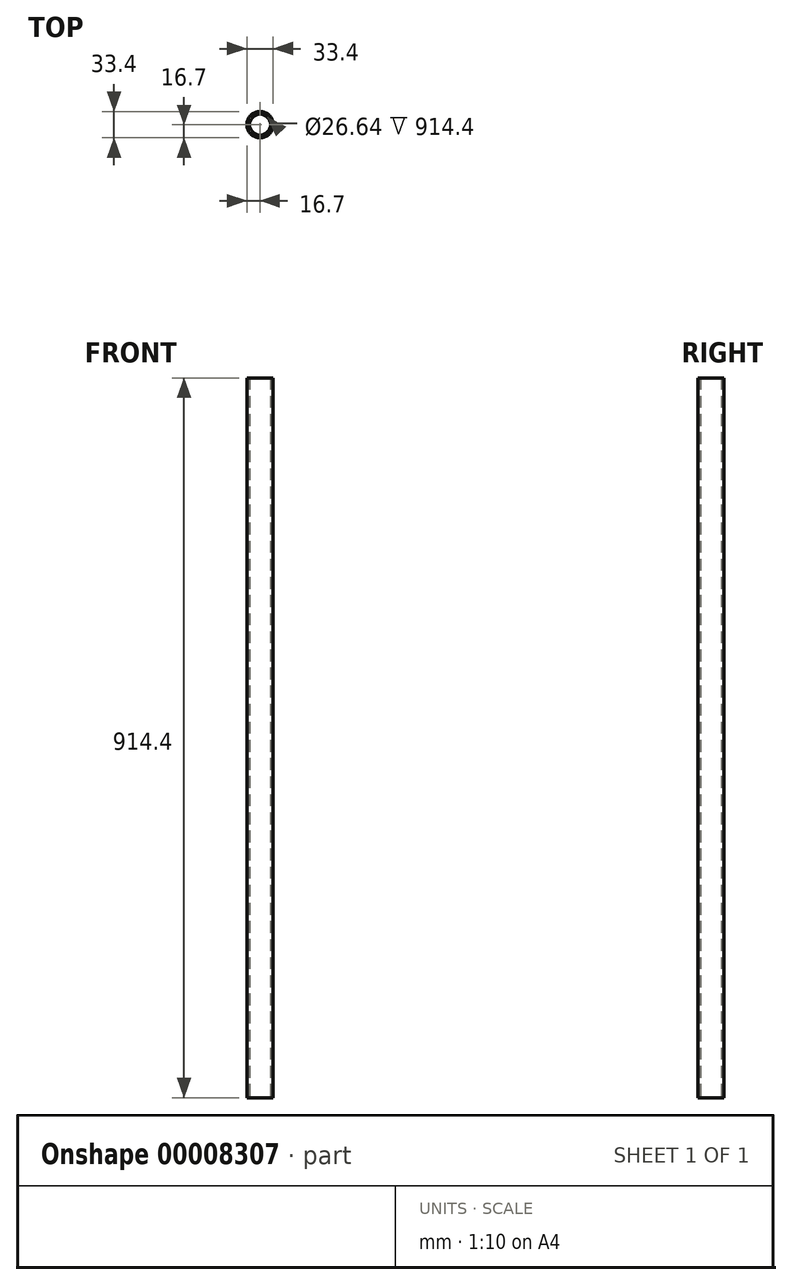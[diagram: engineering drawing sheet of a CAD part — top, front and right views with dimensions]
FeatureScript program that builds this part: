
annotation { "Feature Type Name" : "Feature", "Feature Type Description" : "" }
export const myFeature = defineFeature(function(context is Context, id is Id, definition is map)
    precondition{}
    {
        {
            var Q0;
            Q0=qCreatedBy(makeId("Top.planeOp"),FACE);
            var sketch = newSketch(context, id + "F0", { "sketchPlane" : qUnion([Q0])});
            skCircle(sketch, "E0", {"center": v(0, 0) * mm, "radius": 16.7 * mm});
            skCircle(sketch, "E1", {"center": v(0, 0) * mm, "radius": 13.32 * mm});
            skSolve(sketch);
        }
        {
            var Q0;
            Q0 = qSketchRegion(id + "F0", true);
            extrude(context, id + "F1", {"entities" : qUnion([Q0]), "depth" : 914.4 * mm});
        }
    });
